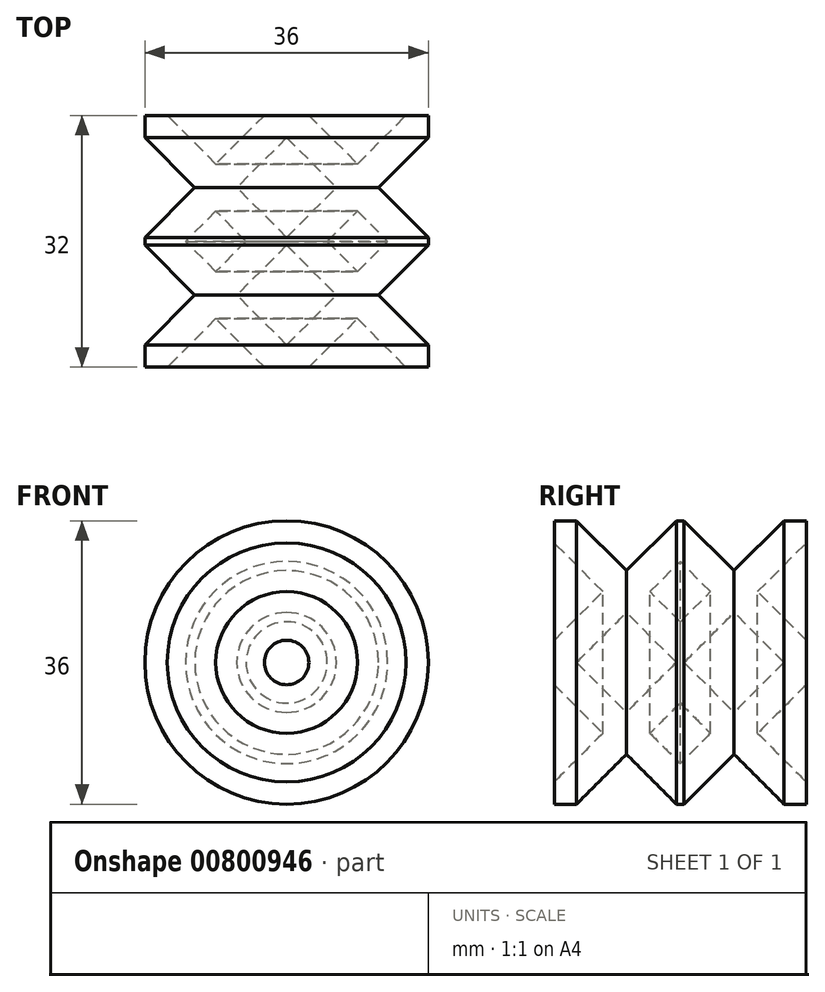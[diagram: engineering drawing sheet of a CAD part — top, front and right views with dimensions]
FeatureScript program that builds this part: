
annotation { "Feature Type Name" : "Feature", "Feature Type Description" : "" }
export const myFeature = defineFeature(function(context is Context, id is Id, definition is map)
    precondition{}
    {
        {
            var Q0;
            Q0=qCreatedBy(makeId("Top.planeOp"),FACE);
            var sketch = newSketch(context, id + "F0", { "sketchPlane" : qUnion([Q0])});
            skLineSegment(sketch, "E0", {"start": v(0, 0) * mm, "end": v(2.83, 0) * mm});
            skLineSegment(sketch, "E1", {"start": v(2.83, 0) * mm, "end": v(9, -6.17) * mm});
            skLineSegment(sketch, "E2", {"start": v(9, -6.17) * mm, "end": v(15.17, 0) * mm});
            skLineSegment(sketch, "E3", {"start": v(15.17, 0) * mm, "end": v(18, 0) * mm});
            skLineSegment(sketch, "E4", {"start": v(18, 0) * mm, "end": v(18, -2.83) * mm});
            skLineSegment(sketch, "E5", {"start": v(18, -2.83) * mm, "end": v(11.66, -9.16) * mm});
            skLineSegment(sketch, "E6", {"start": v(11.66, -22.84) * mm, "end": v(18, -29.17) * mm});
            skLineSegment(sketch, "E7", {"start": v(18, -29.17) * mm, "end": v(18, -32) * mm});
            skLineSegment(sketch, "E8", {"start": v(18, -32) * mm, "end": v(15.17, -32) * mm});
            skLineSegment(sketch, "E9", {"start": v(15.17, -32) * mm, "end": v(9, -25.83) * mm});
            skLineSegment(sketch, "E10", {"start": v(9, -25.83) * mm, "end": v(2.83, -32) * mm});
            skLineSegment(sketch, "E11", {"start": v(2.83, -32) * mm, "end": v(0, -32) * mm});
            skLineSegment(sketch, "E12", {"start": v(0, -32) * mm, "end": v(0, -29.17) * mm});
            skLineSegment(sketch, "E13", {"start": v(0, -29.17) * mm, "end": v(6.34, -22.84) * mm});
            skLineSegment(sketch, "E14", {"start": v(6.34, -22.84) * mm, "end": v(0, -16.5) * mm});
            skLineSegment(sketch, "E15", {"start": v(0, -16.5) * mm, "end": v(0, -15.5) * mm});
            skLineSegment(sketch, "E16", {"start": v(0, -15.5) * mm, "end": v(6.34, -9.16) * mm});
            skLineSegment(sketch, "E17", {"start": v(6.34, -9.16) * mm, "end": v(0, -2.83) * mm});
            skLineSegment(sketch, "E18", {"start": v(0, -2.83) * mm, "end": v(0, 0) * mm});
            skLineSegment(sketch, "E19", {"start": v(11.66, -9.16) * mm, "end": v(18, -15.5) * mm});
            skLineSegment(sketch, "E20", {"start": v(18, -15.5) * mm, "end": v(18, -16.5) * mm});
            skLineSegment(sketch, "E21", {"start": v(18, -16.5) * mm, "end": v(11.66, -22.84) * mm});
            skLineSegment(sketch, "E22", {"start": v(9, -12.16) * mm, "end": v(5.16, -16) * mm});
            skLineSegment(sketch, "E23", {"start": v(5.16, -16) * mm, "end": v(9, -19.84) * mm});
            skLineSegment(sketch, "E24", {"start": v(9, -19.84) * mm, "end": v(12.84, -16) * mm});
            skLineSegment(sketch, "E25", {"start": v(12.84, -16) * mm, "end": v(9, -12.16) * mm});
            skSolve(sketch);
        }
        {
            var Q0;
            Q0=makeQuery(id+"F0.imprint","IMPRINT",FACE,{"disambiguationData":[TD([[makeQuery(id+"F0.imprint","IMPRINT",EDGE,{"derivedFrom":sQuery(id+"F0.wireOp",EDGE,"E0")}),-1.0]])]});
            var Q1;
            Q1=sQuery(id+"F0.wireOp",EDGE,"E18");
            revolve(context, id + "F1", {"surfaceOperationType" : NewSurfaceOperationType.NEW, "entities" : qUnion([Q0]), "axis" : qUnion([Q1]), "revolveType" : RevolveType.FULL});
        }
    });
